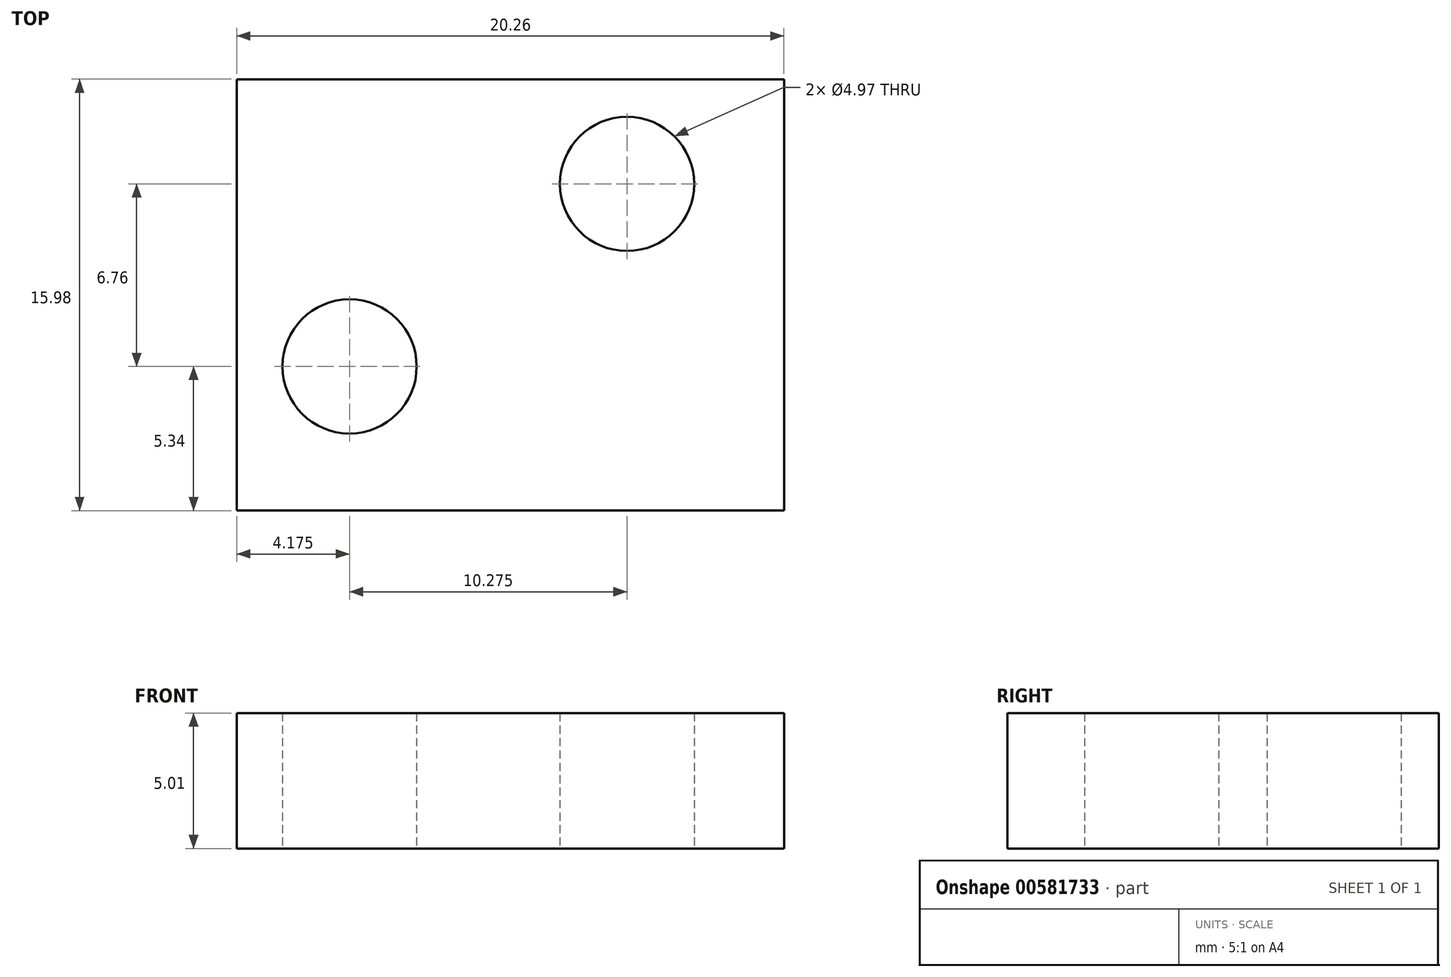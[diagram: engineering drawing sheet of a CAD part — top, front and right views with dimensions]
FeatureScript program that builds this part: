
annotation { "Feature Type Name" : "Feature", "Feature Type Description" : "" }
export const myFeature = defineFeature(function(context is Context, id is Id, definition is map)
    precondition{}
    {
        {
            var Q0;
            Q0=qCreatedBy(makeId("Top.planeOp"),FACE);
            var sketch = newSketch(context, id + "F0", { "sketchPlane" : qUnion([Q0])});
            skLineSegment(sketch, "E0.bottom", {"start": v(-10.13, 7.99) * mm, "end": v(10.14, 7.99) * mm});
            skLineSegment(sketch, "E0.top", {"start": v(-10.14, -7.99) * mm, "end": v(10.13, -7.99) * mm});
            skLineSegment(sketch, "E0.left", {"start": v(-10.13, 7.98) * mm, "end": v(-10.14, -7.99) * mm});
            skLineSegment(sketch, "E0.right", {"start": v(10.14, 7.98) * mm, "end": v(10.13, -7.99) * mm});
            skPoint(sketch, "E0.middle", {"position": v(0, 0) * mm});
            skCircle(sketch, "E1", {"center": v(4.32, 4.11) * mm, "radius": 2.48 * mm});
            skCircle(sketch, "E2", {"center": v(-5.96, -2.65) * mm, "radius": 2.48 * mm});
            skLineSegment(sketch, "E3", {"start": v(1.84, 7.99) * mm, "end": v(1.84, -7.99) * mm, "construction": true});
            skLineSegment(sketch, "E4", {"start": v(-10.13, 1.62) * mm, "end": v(10.13, 1.63) * mm, "construction": true});
            skLineSegment(sketch, "E5", {"start": v(-10.13, -5.14) * mm, "end": v(10.13, -5.13) * mm, "construction": true});
            skLineSegment(sketch, "E6", {"start": v(-8.44, 7.99) * mm, "end": v(-8.44, -7.99) * mm, "construction": true});
            skSolve(sketch);
        }
        {
            var Q0;
            Q0=makeQuery(id+"F0.imprint","IMPRINT",FACE,{"disambiguationData":[TD([[makeQuery(id+"F0.imprint","IMPRINT",EDGE,{"derivedFrom":sQuery(id+"F0.wireOp",EDGE,"E0.bottom")}),-1.0]])]});
            extrude(context, id + "F1", {"entities" : qUnion([Q0]), "depth" : 5 * mm, "offsetDistance" : 25 * mm});
        }
    });
